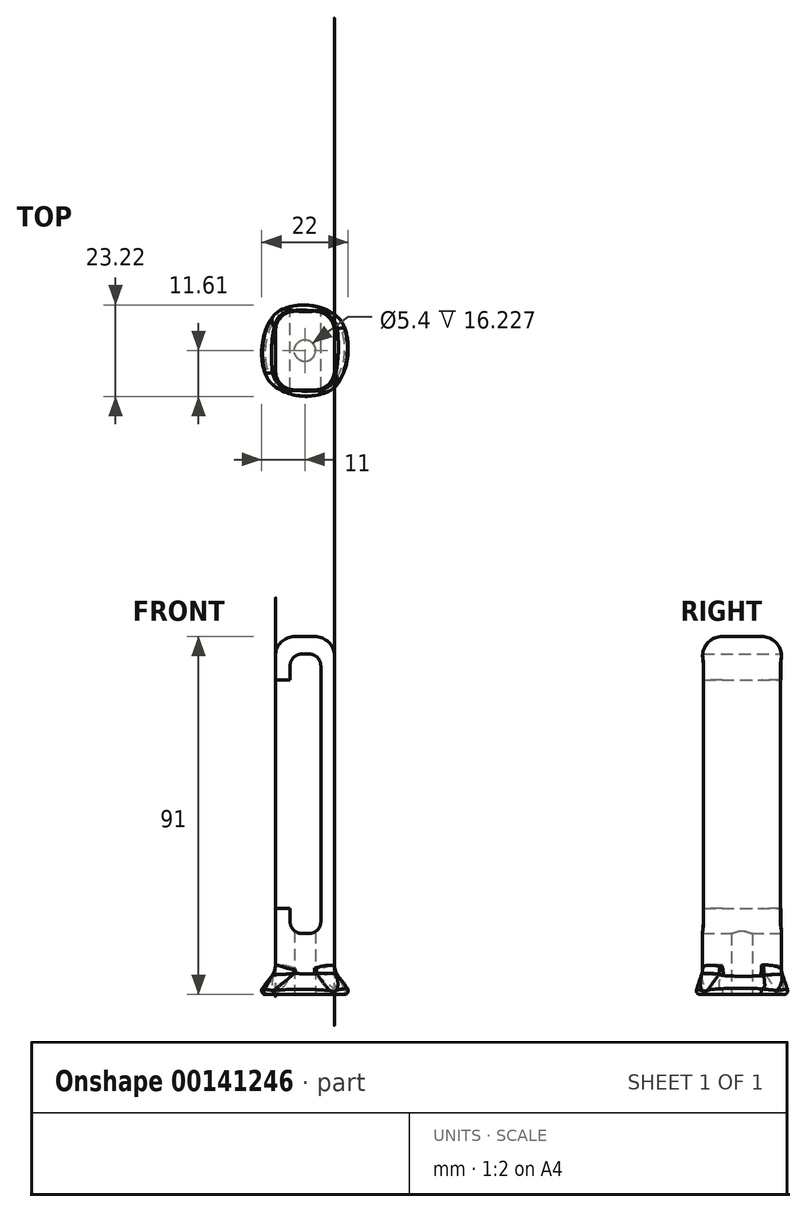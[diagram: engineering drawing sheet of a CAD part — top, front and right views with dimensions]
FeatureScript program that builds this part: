
annotation { "Feature Type Name" : "Feature", "Feature Type Description" : "" }
export const myFeature = defineFeature(function(context is Context, id is Id, definition is map)
    precondition{}
    {
        {
            var Q0;
            Q0=qCreatedBy(makeId("Front.planeOp"),FACE);
            var sketch = newSketch(context, id + "F0", { "sketchPlane" : qUnion([Q0])});
            skLineSegment(sketch, "E0.bottom", {"start": v(-2.5, 42.5) * mm, "end": v(2.5, 42.5) * mm});
            skLineSegment(sketch, "E0.top", {"start": v(-7.5, -42.5) * mm, "end": v(7.5, -42.5) * mm});
            skLineSegment(sketch, "E0.left", {"start": v(-7.5, 37.5) * mm, "end": v(-7.5, 31.48) * mm});
            skLineSegment(sketch, "E0.right", {"start": v(7.5, 37.5) * mm, "end": v(7.5, -42.5) * mm});
            skPoint(sketch, "E0.middle", {"position": v(0, 0) * mm});
            skPoint(sketch, "E1.visualSharp", {"position": v(-7.5, 42.5) * mm});
            skArc(sketch, "E1.filletArc", {"start": v(-2.5, 42.5) * mm, "mid": v(-6.04, 41.04) * mm, "end": v(-7.5, 37.5) * mm});
            skPoint(sketch, "E2.visualSharp", {"position": v(7.5, 42.5) * mm});
            skArc(sketch, "E2.filletArc", {"start": v(7.5, 37.5) * mm, "mid": v(6.04, 41.04) * mm, "end": v(2.5, 42.5) * mm});
            skLineSegment(sketch, "E3.bottom", {"start": v(1.04, 38.02) * mm, "end": v(-0.76, 38.02) * mm});
            skLineSegment(sketch, "E3.top", {"start": v(1.04, -32.98) * mm, "end": v(-0.76, -32.98) * mm});
            skLineSegment(sketch, "E3.left", {"start": v(4.04, 35.02) * mm, "end": v(4.04, -29.98) * mm});
            skLineSegment(sketch, "E3.right", {"start": v(-3.76, 35.02) * mm, "end": v(-3.76, 31.48) * mm});
            skPoint(sketch, "E4.visualSharp", {"position": v(-3.76, 38.02) * mm});
            skArc(sketch, "E4.filletArc", {"start": v(-0.76, 38.02) * mm, "mid": v(-2.89, 37.14) * mm, "end": v(-3.76, 35.02) * mm});
            skPoint(sketch, "E5.visualSharp", {"position": v(4.04, 38.02) * mm});
            skArc(sketch, "E5.filletArc", {"start": v(4.04, 35.02) * mm, "mid": v(3.16, 37.14) * mm, "end": v(1.04, 38.02) * mm});
            skPoint(sketch, "E6.visualSharp", {"position": v(-3.76, -32.98) * mm});
            skArc(sketch, "E6.filletArc", {"start": v(-3.76, -29.98) * mm, "mid": v(-2.89, -32.1) * mm, "end": v(-0.76, -32.98) * mm});
            skPoint(sketch, "E7.visualSharp", {"position": v(4.04, -32.98) * mm});
            skArc(sketch, "E7.filletArc", {"start": v(1.04, -32.98) * mm, "mid": v(3.16, -32.1) * mm, "end": v(4.04, -29.98) * mm});
            skLineSegment(sketch, "E8.bottom", {"start": v(-7.5, 31.48) * mm, "end": v(-3.76, 31.48) * mm});
            skLineSegment(sketch, "E8.top", {"start": v(-7.5, -26.64) * mm, "end": v(-3.76, -26.64) * mm});
            skLineSegment(sketch, "E9.trimOffspring", {"start": v(-7.5, -26.64) * mm, "end": v(-7.5, -42.5) * mm});
            skLineSegment(sketch, "E10.trimOffspring", {"start": v(-3.76, -26.64) * mm, "end": v(-3.76, -29.98) * mm});
            skSolve(sketch);
        }
        {
            var Q0;
            Q0 = qSketchRegion(id + "F0", true);
            extrude(context, id + "F1", {"entities" : qUnion([Q0]), "endBound" : BoundingType.SYMMETRIC, "depth" : 20 * mm});
        }
        {
            var Q0;
            Q0=makeQuery(id+"F1.opExtrude","SWEPT_FACE",FACE,{"disambiguationData":[OSD([sQuery(id+"F0.wireOp",EDGE,"E0.top")])]});
            cPlane(context, id + "F2", {"entities" : qUnion([Q0]), "cplaneType" : CPlaneType.OFFSET, "offset" : 6 * mm, "width" : 150 * mm, "height" : 150 * mm});
        }
        {
            var Q0;
            Q0=qCreatedBy(id+"F2.planeOp",FACE);
            var sketch = newSketch(context, id + "F3", { "sketchPlane" : qUnion([Q0])});
            skCircle(sketch, "E11", {"center": v(0, 0) * mm, "radius": 12 * mm});
            skSolve(sketch);
        }
        {
            var Q0;
            Q0=makeQuery(id+"F3.imprint","IMPRINT",FACE,{"disambiguationData":[TD([[makeQuery(id+"F3.imprint","IMPRINT",EDGE,{"derivedFrom":sQuery(id+"F3.wireOp",EDGE,"E11")}),1.0]])]});
            var Q1;
            Q1=makeQuery(id+"F1.opExtrude","SWEPT_FACE",FACE,{"disambiguationData":[OSD([sQuery(id+"F0.wireOp",EDGE,"E0.top")])]});
            loft(context, id + "F4", {"operationType" : NewBodyOperationType.ADD, "sheetProfilesArray" : [{ "sheetProfileEntities" : qUnion([Q0]) }, { "sheetProfileEntities" : qUnion([Q1]) }]});
        }
        {
            var Q0;
            {var subQ0=sQuery(id+"F3.wireOp",EDGE,"E11");var subQ1=sQuery(id+"F0.wireOp",EDGE,"E9.trimOffspring");var subQ2=sQuery(id+"F0.wireOp",EDGE,"E0.top");Q0=makeQuery(id+"F4.opLoft","MID_CAP_EDGE",EDGE,{"disambiguationData":[OSD([subQ2,subQ1,subQ0]),TDD([makeQuery(id+"F1.opExtrude","CAP_VERTEX",VERTEX,{"disambiguationData":[OSD([subQ2,subQ1])],"isStart":true}),makeQuery(id+"F3.imprint","IMPRINT",EDGE,{"derivedFrom":subQ0})])],"capPos":0.0});}
            var Q1;
            {var subQ0=sQuery(id+"F3.wireOp",EDGE,"E11");var subQ1=sQuery(id+"F0.wireOp",EDGE,"E0.right");var subQ2=sQuery(id+"F0.wireOp",EDGE,"E0.top");var subQ3=sQuery(id+"F0.wireOp",EDGE,"E9.trimOffspring");Q1=makeQuery(id+"F4.opLoft","MID_CAP_EDGE",EDGE,{"disambiguationData":[OSD([subQ2,subQ1,subQ3,subQ0]),TDD([makeQuery(id+"F1.opExtrude","CAP_VERTEX",VERTEX,{"disambiguationData":[OSD([subQ2,subQ3])],"isStart":true}),makeQuery(id+"F1.opExtrude","CAP_VERTEX",VERTEX,{"disambiguationData":[OSD([subQ2,subQ1])],"isStart":false}),makeQuery(id+"F3.imprint","IMPRINT",EDGE,{"derivedFrom":subQ0})])],"capPos":0.0});}
            var Q2;
            {var subQ0=sQuery(id+"F3.wireOp",EDGE,"E11");var subQ1=sQuery(id+"F0.wireOp",EDGE,"E0.right");var subQ2=sQuery(id+"F0.wireOp",EDGE,"E0.top");var subQ3=sQuery(id+"F0.wireOp",EDGE,"E9.trimOffspring");Q2=makeQuery(id+"F4.opLoft","MID_CAP_EDGE",EDGE,{"disambiguationData":[OSD([subQ2,subQ1,subQ3,subQ0]),TDD([makeQuery(id+"F1.opExtrude","CAP_VERTEX",VERTEX,{"disambiguationData":[OSD([subQ2,subQ3])],"isStart":false}),makeQuery(id+"F1.opExtrude","CAP_VERTEX",VERTEX,{"disambiguationData":[OSD([subQ2,subQ1])],"isStart":false}),makeQuery(id+"F3.imprint","IMPRINT",EDGE,{"derivedFrom":subQ0})])],"capPos":0.0});}
            var Q3;
            {var subQ0=sQuery(id+"F3.wireOp",EDGE,"E11");var subQ1=sQuery(id+"F0.wireOp",EDGE,"E9.trimOffspring");var subQ2=sQuery(id+"F0.wireOp",EDGE,"E0.top");Q3=makeQuery(id+"F4.opLoft","MID_CAP_EDGE",EDGE,{"disambiguationData":[OSD([subQ2,subQ1,subQ0]),TDD([makeQuery(id+"F1.opExtrude","CAP_VERTEX",VERTEX,{"disambiguationData":[OSD([subQ2,subQ1])],"isStart":true}),makeQuery(id+"F1.opExtrude","CAP_VERTEX",VERTEX,{"disambiguationData":[OSD([subQ2,subQ1])],"isStart":false}),makeQuery(id+"F3.imprint","IMPRINT",EDGE,{"derivedFrom":subQ0})])],"capPos":0.0});}
            fillet(context, id + "F5", {"entities" : qUnion([Q0, Q1, Q2, Q3]), "radius" : 1 * mm, "allowEdgeOverflow" : false});
        }
        {
            var Q0;
            Q0=makeQuery(id+"F1.opExtrude","CAP_EDGE",EDGE,{"disambiguationData":[OSD([sQuery(id+"F0.wireOp",EDGE,"E9.trimOffspring")])],"isStart":false});
            var Q1;
            Q1=makeQuery(id+"F1.opExtrude","CAP_EDGE",EDGE,{"disambiguationData":[OSD([sQuery(id+"F0.wireOp",EDGE,"E9.trimOffspring")])],"isStart":true});
            var Q2;
            Q2=makeQuery(id+"F1.opExtrude","CAP_EDGE",EDGE,{"disambiguationData":[OSD([sQuery(id+"F0.wireOp",EDGE,"E0.right")])],"isStart":false});
            var Q3;
            Q3=makeQuery(id+"F1.opExtrude","CAP_EDGE",EDGE,{"disambiguationData":[OSD([sQuery(id+"F0.wireOp",EDGE,"E0.right")])],"isStart":true});
            var Q4;
            Q4=makeQuery(id+"F4.opLoft","SWEPT_EDGE",EDGE,{"disambiguationData":[OSD([sQuery(id+"F0.wireOp",EDGE,"E0.top"),sQuery(id+"F0.wireOp",EDGE,"E0.right"),sQuery(id+"F0.wireOp",EDGE,"E9.trimOffspring"),sQuery(id+"F3.wireOp",EDGE,"E11")])]});
            var Q5;
            Q5=makeQuery(id+"F4.opLoft","SWEPT_EDGE",EDGE,{"disambiguationData":[OSD([sQuery(id+"F0.wireOp",EDGE,"E0.top"),sQuery(id+"F0.wireOp",EDGE,"E9.trimOffspring"),sQuery(id+"F3.wireOp",EDGE,"E11")])]});
            var Q6;
            Q6=makeQuery(id+"F4.opLoft","SWEPT_EDGE",EDGE,{"disambiguationData":[OSD([sQuery(id+"F0.wireOp",EDGE,"E0.top"),sQuery(id+"F0.wireOp",EDGE,"E9.trimOffspring")])]});
            var Q7;
            Q7=makeQuery(id+"F4.opLoft","SWEPT_EDGE",EDGE,{"disambiguationData":[OSD([sQuery(id+"F0.wireOp",EDGE,"E0.top"),sQuery(id+"F0.wireOp",EDGE,"E0.right"),sQuery(id+"F3.wireOp",EDGE,"E11")])]});
            fillet(context, id + "F6", {"entities" : qUnion([Q0, Q1, Q2, Q3, Q4, Q5, Q6, Q7]), "radius" : 5 * mm, "tangentPropagation" : true, "allowEdgeOverflow" : false});
        }
        {
            var Q0;
            Q0=makeQuery(id+"F4.opLoft","CAP_FACE",FACE,{"disambiguationData":[OSD([makeQuery(id+"F3.imprint","IMPRINT",FACE,{"disambiguationData":[TD([[makeQuery(id+"F3.imprint","IMPRINT",EDGE,{"derivedFrom":sQuery(id+"F3.wireOp",EDGE,"E11")}),1.0]])]})])],"isStart":true});
            var sketch = newSketch(context, id + "F7", { "sketchPlane" : qUnion([Q0])});
            skCircle(sketch, "E12", {"center": v(0, 0) * mm, "radius": 2.7 * mm});
            skSolve(sketch);
        }
        {
            var Q0;
            Q0 = qSketchRegion(id + "F7", true);
            extrude(context, id + "F8", {"entities" : qUnion([Q0]), "operationType" : NewBodyOperationType.REMOVE, "endBound" : BoundingType.UP_TO_NEXT, "oppositeDirection" : true, "depth" : 25 * mm});
        }
        {
            var Q0;
            {var subQ0=sQuery(id+"F0.wireOp",EDGE,"E0.top");var subQ1=makeQuery(id+"F1.opExtrude","CAP_EDGE",EDGE,{"disambiguationData":[OSD([subQ0])],"isStart":false});var subQ2=sQuery(id+"F0.wireOp",EDGE,"E0.right");var subQ3=sQuery(id+"F0.wireOp",EDGE,"E9.trimOffspring");Q0=makeQuery(id+"F4.boolean.opBoolean","MERGE",EDGE,{"derivedFrom":[subQ1,makeQuery(id+"F4.opLoft","MID_CAP_EDGE",EDGE,{"disambiguationData":[OSD([subQ0,subQ2,subQ3]),TDD([makeQuery(id+"F1.opExtrude","CAP_VERTEX",VERTEX,{"disambiguationData":[OSD([subQ0,subQ3])],"isStart":false}),makeQuery(id+"F1.opExtrude","CAP_VERTEX",VERTEX,{"disambiguationData":[OSD([subQ0,subQ2])],"isStart":false}),subQ1])],"capPos":1.0})]});}
            var Q1;
            {var subQ0=sQuery(id+"F0.wireOp",EDGE,"E9.trimOffspring");Q1=makeQuery(id+"F6.opFillet","BLEND_EDGE",EDGE,{"blendedFrom":[makeQuery(id+"F1.opExtrude","CAP_EDGE",EDGE,{"disambiguationData":[OSD([subQ0])],"isStart":false}),makeQuery(id+"F4.opLoft","SWEPT_EDGE",EDGE,{"disambiguationData":[OSD([sQuery(id+"F0.wireOp",EDGE,"E0.top"),subQ0,sQuery(id+"F3.wireOp",EDGE,"E11")])]})],"blendedInto":[]});}
            var Q2;
            {var subQ0=sQuery(id+"F0.wireOp",EDGE,"E9.trimOffspring");var subQ1=sQuery(id+"F0.wireOp",EDGE,"E0.top");Q2=makeQuery(id+"F6.opFillet","BLEND_EDGE",EDGE,{"blendedFrom":[makeQuery(id+"F4.opLoft","SWEPT_EDGE",EDGE,{"disambiguationData":[OSD([subQ1,subQ0,sQuery(id+"F3.wireOp",EDGE,"E11")])]}),makeQuery(id+"F1.opExtrude","CAP_FACE",FACE,{"disambiguationData":[OSD([sQuery(id+"F0.wireOp",EDGE,"E0.bottom"),subQ1,sQuery(id+"F0.wireOp",EDGE,"E0.left"),sQuery(id+"F0.wireOp",EDGE,"E0.right"),sQuery(id+"F0.wireOp",EDGE,"E1.filletArc"),sQuery(id+"F0.wireOp",EDGE,"E2.filletArc"),sQuery(id+"F0.wireOp",EDGE,"E3.bottom"),sQuery(id+"F0.wireOp",EDGE,"E3.top"),sQuery(id+"F0.wireOp",EDGE,"E3.left"),sQuery(id+"F0.wireOp",EDGE,"E3.right"),sQuery(id+"F0.wireOp",EDGE,"E4.filletArc"),sQuery(id+"F0.wireOp",EDGE,"E5.filletArc"),sQuery(id+"F0.wireOp",EDGE,"E6.filletArc"),sQuery(id+"F0.wireOp",EDGE,"E7.filletArc"),sQuery(id+"F0.wireOp",EDGE,"E8.bottom"),sQuery(id+"F0.wireOp",EDGE,"E8.top"),subQ0,sQuery(id+"F0.wireOp",EDGE,"E10.trimOffspring")])],"isStart":false})],"blendedInto":[makeQuery(id+"F1.opExtrude","CAP_FACE",FACE,{"disambiguationData":[OSD([sQuery(id+"F0.wireOp",EDGE,"E0.bottom"),subQ1,sQuery(id+"F0.wireOp",EDGE,"E0.left"),sQuery(id+"F0.wireOp",EDGE,"E0.right"),sQuery(id+"F0.wireOp",EDGE,"E1.filletArc"),sQuery(id+"F0.wireOp",EDGE,"E2.filletArc"),sQuery(id+"F0.wireOp",EDGE,"E3.bottom"),sQuery(id+"F0.wireOp",EDGE,"E3.top"),sQuery(id+"F0.wireOp",EDGE,"E3.left"),sQuery(id+"F0.wireOp",EDGE,"E3.right"),sQuery(id+"F0.wireOp",EDGE,"E4.filletArc"),sQuery(id+"F0.wireOp",EDGE,"E5.filletArc"),sQuery(id+"F0.wireOp",EDGE,"E6.filletArc"),sQuery(id+"F0.wireOp",EDGE,"E7.filletArc"),sQuery(id+"F0.wireOp",EDGE,"E8.bottom"),sQuery(id+"F0.wireOp",EDGE,"E8.top"),subQ0,sQuery(id+"F0.wireOp",EDGE,"E10.trimOffspring")])],"isStart":false})]});}
            var Q3;
            {var subQ0=sQuery(id+"F0.wireOp",EDGE,"E0.right");Q3=makeQuery(id+"F6.opFillet","BLEND_EDGE",EDGE,{"blendedFrom":[makeQuery(id+"F1.opExtrude","CAP_EDGE",EDGE,{"disambiguationData":[OSD([subQ0])],"isStart":false}),makeQuery(id+"F4.opLoft","SWEPT_EDGE",EDGE,{"disambiguationData":[OSD([sQuery(id+"F0.wireOp",EDGE,"E0.top"),subQ0,sQuery(id+"F0.wireOp",EDGE,"E9.trimOffspring"),sQuery(id+"F3.wireOp",EDGE,"E11")])]})],"blendedInto":[]});}
            var Q4;
            {var subQ0=sQuery(id+"F3.wireOp",EDGE,"E11");var subQ1=sQuery(id+"F0.wireOp",EDGE,"E0.top");var subQ2=sQuery(id+"F0.wireOp",EDGE,"E0.right");var subQ3=sQuery(id+"F0.wireOp",EDGE,"E9.trimOffspring");Q4=makeQuery(id+"F6.opFillet","BLEND_EDGE",EDGE,{"blendedFrom":[makeQuery(id+"F1.opExtrude","CAP_EDGE",EDGE,{"disambiguationData":[OSD([subQ2])],"isStart":false}),makeQuery(id+"F4.opLoft","SWEPT_FACE",FACE,{"disambiguationData":[OSD([subQ1,subQ2,subQ3,subQ0]),TDD([makeQuery(id+"F1.opExtrude","CAP_VERTEX",VERTEX,{"disambiguationData":[OSD([subQ1,subQ3])],"isStart":true}),makeQuery(id+"F1.opExtrude","CAP_VERTEX",VERTEX,{"disambiguationData":[OSD([subQ1,subQ3])],"isStart":false}),makeQuery(id+"F1.opExtrude","CAP_VERTEX",VERTEX,{"disambiguationData":[OSD([subQ1,subQ2])],"isStart":false}),makeQuery(id+"F1.opExtrude","CAP_EDGE",EDGE,{"disambiguationData":[OSD([subQ1])],"isStart":false}),makeQuery(id+"F3.imprint","IMPRINT",EDGE,{"derivedFrom":subQ0})])]})],"blendedInto":[makeQuery(id+"F4.opLoft","SWEPT_FACE",FACE,{"disambiguationData":[OSD([subQ1,subQ2,subQ3,subQ0]),TDD([makeQuery(id+"F1.opExtrude","CAP_VERTEX",VERTEX,{"disambiguationData":[OSD([subQ1,subQ3])],"isStart":true}),makeQuery(id+"F1.opExtrude","CAP_VERTEX",VERTEX,{"disambiguationData":[OSD([subQ1,subQ3])],"isStart":false}),makeQuery(id+"F1.opExtrude","CAP_VERTEX",VERTEX,{"disambiguationData":[OSD([subQ1,subQ2])],"isStart":false}),makeQuery(id+"F1.opExtrude","CAP_EDGE",EDGE,{"disambiguationData":[OSD([subQ1])],"isStart":false}),makeQuery(id+"F3.imprint","IMPRINT",EDGE,{"derivedFrom":subQ0})])]})]});}
            fillet(context, id + "F9", {"entities" : qUnion([Q0, Q1, Q2, Q3, Q4]), "radius" : 5 * mm, "tangentPropagation" : true, "allowEdgeOverflow" : false});
        }
    });
